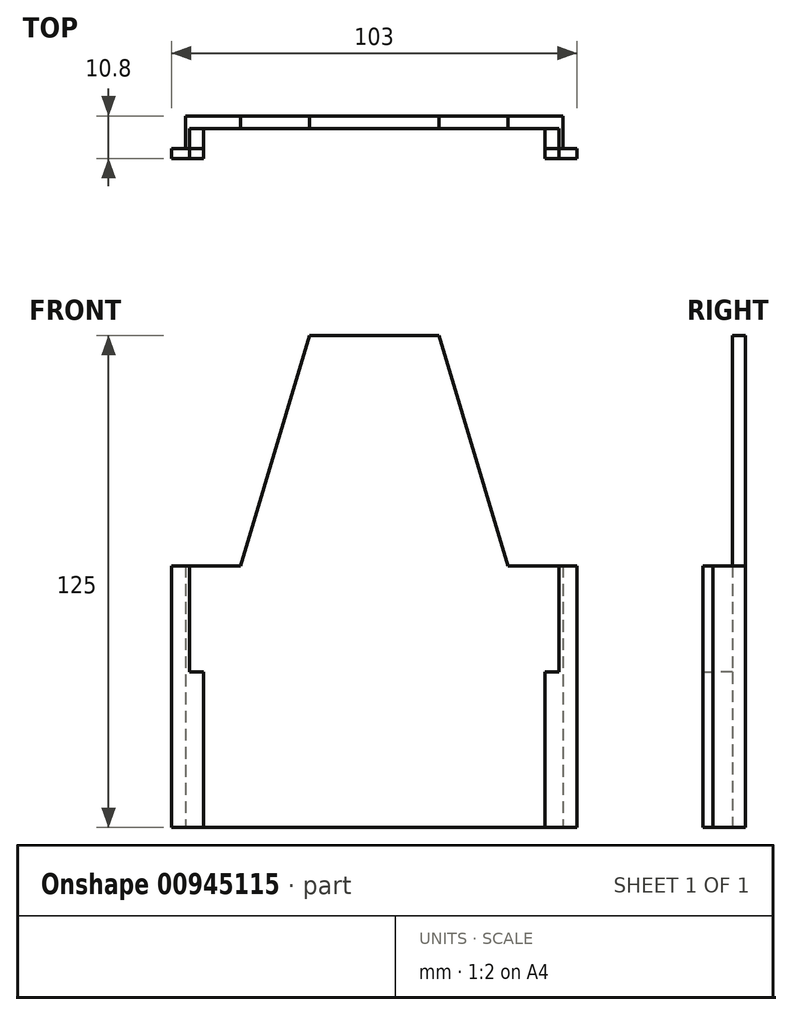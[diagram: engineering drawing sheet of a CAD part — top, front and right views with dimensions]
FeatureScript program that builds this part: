
annotation { "Feature Type Name" : "Feature", "Feature Type Description" : "" }
export const myFeature = defineFeature(function(context is Context, id is Id, definition is map)
    precondition{}
    {
        {
            var Q0;
            Q0=qCreatedBy(makeId("Front.planeOp"),FACE);
            var sketch = newSketch(context, id + "F0", { "sketchPlane" : qUnion([Q0])});
            skLineSegment(sketch, "E0.bottom", {"start": v(-25.95, 21.71) * mm, "end": v(77.05, 21.71) * mm});
            skLineSegment(sketch, "E0.top", {"start": v(-25.95, -44.79) * mm, "end": v(77.05, -44.79) * mm});
            skLineSegment(sketch, "E0.left", {"start": v(-25.95, 21.71) * mm, "end": v(-25.95, -44.79) * mm});
            skLineSegment(sketch, "E0.right", {"start": v(77.05, 21.71) * mm, "end": v(77.05, -44.79) * mm});
            skLineSegment(sketch, "E1", {"start": v(-25.95, 21.71) * mm, "end": v(-22.36, 21.71) * mm});
            skLineSegment(sketch, "E2", {"start": v(-22.36, 21.71) * mm, "end": v(-22.36, -44.79) * mm});
            skLineSegment(sketch, "E3", {"start": v(25.55, 21.71) * mm, "end": v(25.55, -44.79) * mm});
            skLineSegment(sketch, "E4", {"start": v(25.55, 21.71) * mm, "end": v(-17.85, 21.71) * mm});
            skLineSegment(sketch, "E5", {"start": v(-17.85, 21.71) * mm, "end": v(-17.85, -44.79) * mm});
            skLineSegment(sketch, "E6", {"start": v(-17.85, 21.71) * mm, "end": v(-21.35, 21.71) * mm});
            skLineSegment(sketch, "E7", {"start": v(-21.35, 21.71) * mm, "end": v(-21.35, -5.29) * mm});
            skLineSegment(sketch, "E8", {"start": v(-21.35, -5.29) * mm, "end": v(-17.85, -5.29) * mm});
            skLineSegment(sketch, "E9.MirrorCS", {"start": v(68.95, 21.71) * mm, "end": v(68.95, -44.79) * mm});
            skLineSegment(sketch, "E10.MirrorCS", {"start": v(72.45, -5.29) * mm, "end": v(68.95, -5.29) * mm});
            skLineSegment(sketch, "E11.MirrorCS", {"start": v(72.45, 21.71) * mm, "end": v(72.45, -5.29) * mm});
            skLineSegment(sketch, "E12.MirrorCS", {"start": v(68.95, 21.71) * mm, "end": v(72.45, 21.71) * mm});
            skLineSegment(sketch, "E13.MirrorCS", {"start": v(73.47, 21.71) * mm, "end": v(73.47, -44.79) * mm});
            skSolve(sketch);
        }
        {
            var Q0;
            {var subQ0=sQuery(id+"F0.wireOp",EDGE,"E0.left");Q0=makeQuery(id+"F0.imprint","IMPRINT",FACE,{"disambiguationData":[TD([[makeQuery(id+"F0.imprint","IMPRINT",EDGE,{"derivedFrom":subQ0}),1.0]])]});}
            var Q1;
            {var subQ0=sQuery(id+"F0.wireOp",EDGE,"E0.right");Q1=makeQuery(id+"F0.imprint","IMPRINT",FACE,{"disambiguationData":[TD([[makeQuery(id+"F0.imprint","IMPRINT",EDGE,{"derivedFrom":subQ0}),-1.0]])]});}
            var Q2;
            {var subQ4=sQuery(id+"F0.wireOp",EDGE,"E2");Q2=makeQuery(id+"F0.imprint","IMPRINT",FACE,{"disambiguationData":[TD([[makeQuery(id+"F0.imprint","IMPRINT",EDGE,{"derivedFrom":subQ4}),1.0]])]});}
            var Q3;
            {var subQ0=sQuery(id+"F0.wireOp",EDGE,"E10.MirrorCS");Q3=makeQuery(id+"F0.imprint","IMPRINT",FACE,{"disambiguationData":[TD([[makeQuery(id+"F0.imprint","IMPRINT",EDGE,{"derivedFrom":subQ0}),1.0]])]});}
            extrude(context, id + "F1", {"entities" : qUnion([Q0, Q1, Q2, Q3]), "depth" : 2.5 * mm, "offsetDistance" : 25 * mm});
        }
        {
            var Q0;
            {var subQ4=sQuery(id+"F0.wireOp",EDGE,"E2");Q0=makeQuery(id+"F0.imprint","IMPRINT",FACE,{"disambiguationData":[TD([[makeQuery(id+"F0.imprint","IMPRINT",EDGE,{"derivedFrom":subQ4}),1.0]])]});}
            var Q1;
            {var subQ0=sQuery(id+"F0.wireOp",EDGE,"E10.MirrorCS");Q1=makeQuery(id+"F0.imprint","IMPRINT",FACE,{"disambiguationData":[TD([[makeQuery(id+"F0.imprint","IMPRINT",EDGE,{"derivedFrom":subQ0}),1.0]])]});}
            extrude(context, id + "F2", {"entities" : qUnion([Q0, Q1]), "oppositeDirection" : true, "depth" : 8.3 * mm, "offsetDistance" : 25 * mm});
        }
        {
            var Q0;
            Q0=makeQuery(id+"F2.opExtrude","CAP_FACE",FACE,{"disambiguationData":[OSD([sQuery(id+"F0.wireOp",EDGE,"E0.bottom"),sQuery(id+"F0.wireOp",EDGE,"E0.top"),sQuery(id+"F0.wireOp",EDGE,"E2"),sQuery(id+"F0.wireOp",EDGE,"E5"),sQuery(id+"F0.wireOp",EDGE,"E7"),sQuery(id+"F0.wireOp",EDGE,"E8")])],"isStart":false});
            var sketch = newSketch(context, id + "F3", { "sketchPlane" : qUnion([Q0])});
            skLineSegment(sketch, "E14.left", {"start": v(22.36, 21.71) * mm, "end": v(22.36, -44.79) * mm});
            skLineSegment(sketch, "E15", {"start": v(22.36, 21.71) * mm, "end": v(-73.47, 21.71) * mm});
            skLineSegment(sketch, "E16", {"start": v(-73.47, 21.71) * mm, "end": v(-73.47, -44.79) * mm});
            skLineSegment(sketch, "E17", {"start": v(-73.47, -44.79) * mm, "end": v(22.36, -44.79) * mm});
            skLineSegment(sketch, "E18", {"start": v(-25.55, -44.79) * mm, "end": v(-25.55, 80.21) * mm});
            skLineSegment(sketch, "E19", {"start": v(-25.55, 80.21) * mm, "end": v(-42.05, 80.21) * mm});
            skLineSegment(sketch, "E20", {"start": v(-25.55, 21.71) * mm, "end": v(-59.55, 21.71) * mm});
            skLineSegment(sketch, "E21", {"start": v(-59.55, 21.71) * mm, "end": v(-42.05, 80.21) * mm});
            skLineSegment(sketch, "E22.MirrorCS", {"start": v(8.45, 21.71) * mm, "end": v(-9.05, 80.21) * mm});
            skLineSegment(sketch, "E23.MirrorCS", {"start": v(-25.55, 80.21) * mm, "end": v(-9.05, 80.21) * mm});
            skSolve(sketch);
        }
        {
            var Q0;
            {var subQ5=makeQuery(id+"F2.opExtrude","CAP_EDGE",EDGE,{"disambiguationData":[OSD([sQuery(id+"F0.wireOp",EDGE,"E5")])],"isStart":false});Q0=makeQuery(id+"F3.imprint","IMPRINT",FACE,{"disambiguationData":[TD([[makeQuery(id+"F3.imprint","IMPRINT",EDGE,{"derivedFrom":subQ5}),-1.0]])]});}
            var Q1;
            {var subQ3=sQuery(id+"F3.wireOp",EDGE,"E22.MirrorCS");Q1=makeQuery(id+"F3.imprint","IMPRINT",FACE,{"disambiguationData":[TD([[makeQuery(id+"F3.imprint","IMPRINT",EDGE,{"derivedFrom":subQ3}),1.0]])]});}
            var Q2;
            {var subQ0=sQuery(id+"F3.wireOp",EDGE,"E19");Q2=makeQuery(id+"F3.imprint","IMPRINT",FACE,{"disambiguationData":[TD([[makeQuery(id+"F3.imprint","IMPRINT",EDGE,{"derivedFrom":subQ0}),1.0]])]});}
            var Q3;
            {var subQ1=sQuery(id+"F3.wireOp",EDGE,"E16");Q3=makeQuery(id+"F3.imprint","IMPRINT",FACE,{"disambiguationData":[TD([[makeQuery(id+"F3.imprint","IMPRINT",EDGE,{"derivedFrom":subQ1}),1.0]])]});}
            extrude(context, id + "F4", {"entities" : qUnion([Q0, Q1, Q2, Q3]), "operationType" : NewBodyOperationType.ADD, "oppositeDirection" : true, "depth" : 3.25 * mm, "offsetDistance" : 25 * mm});
        }
    });
